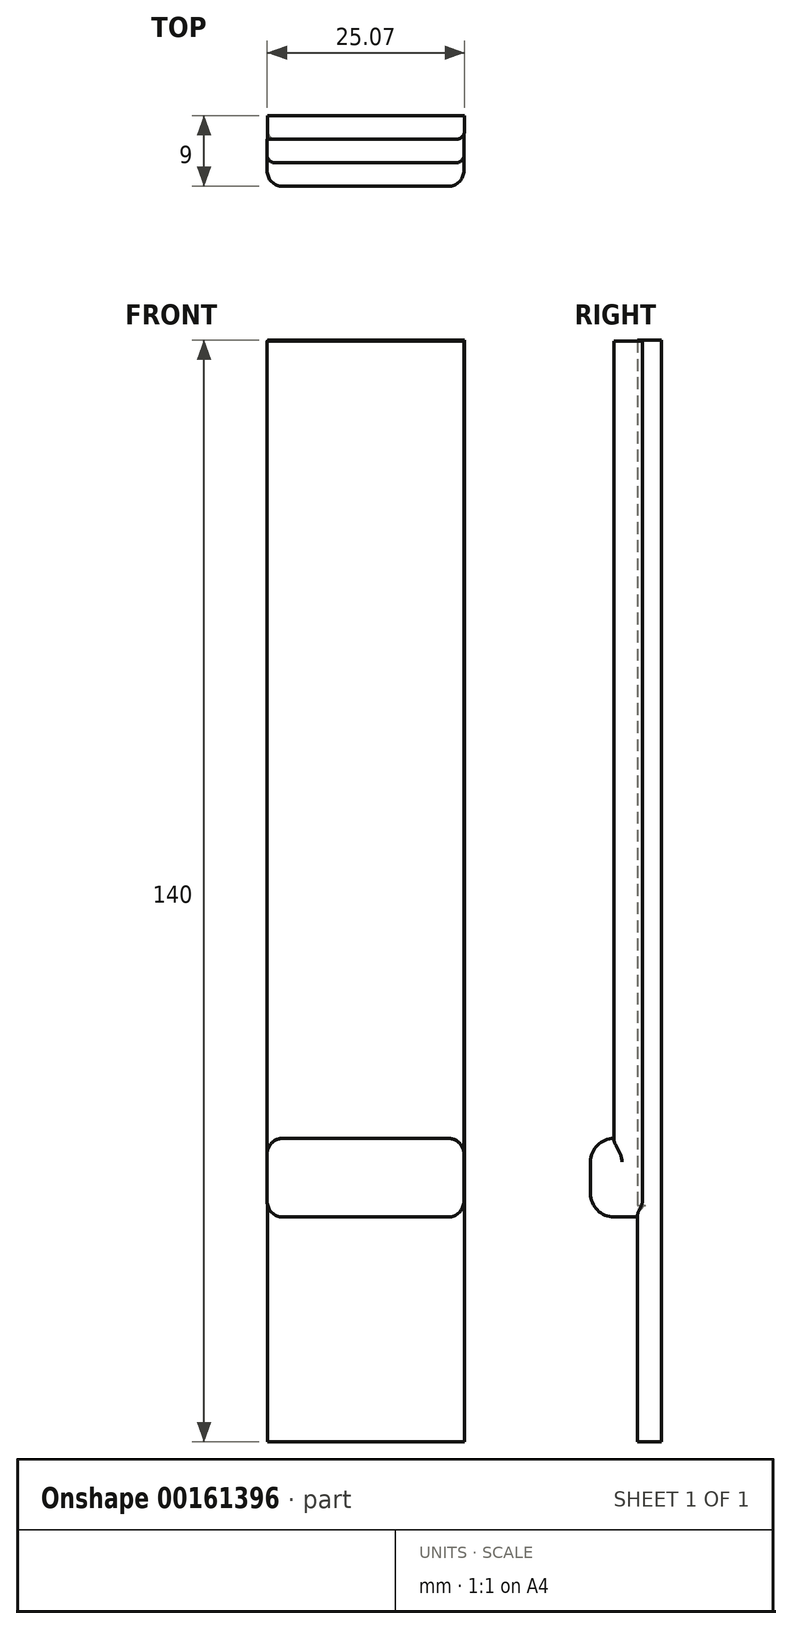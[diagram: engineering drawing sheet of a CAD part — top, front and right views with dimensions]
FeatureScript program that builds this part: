
annotation { "Feature Type Name" : "Feature", "Feature Type Description" : "" }
export const myFeature = defineFeature(function(context is Context, id is Id, definition is map)
    precondition{}
    {
        {
            var Q0;
            Q0=qCreatedBy(makeId("Front.planeOp"),FACE);
            var sketch = newSketch(context, id + "F0", { "sketchPlane" : qUnion([Q0])});
            skLineSegment(sketch, "E0.bottom", {"start": v(-25.63, 65.25) * mm, "end": v(-0.63, 65.25) * mm});
            skLineSegment(sketch, "E0.top", {"start": v(-25.63, -74.75) * mm, "end": v(-0.63, -74.75) * mm});
            skLineSegment(sketch, "E0.left", {"start": v(-25.63, 65.25) * mm, "end": v(-25.63, -74.75) * mm});
            skLineSegment(sketch, "E0.right", {"start": v(-0.63, 65.25) * mm, "end": v(-0.63, -74.75) * mm});
            skSolve(sketch);
        }
        {
            var Q0;
            Q0 = qSketchRegion(id + "F0", true);
            extrude(context, id + "F1", {"entities" : qUnion([Q0]), "depth" : 3 * mm});
        }
        {
            var Q0;
            Q0=makeQuery(id+"F1.opExtrude","CAP_FACE",FACE,{"disambiguationData":[OSD([sQuery(id+"F0.wireOp",EDGE,"E0.bottom"),sQuery(id+"F0.wireOp",EDGE,"E0.top"),sQuery(id+"F0.wireOp",EDGE,"E0.left"),sQuery(id+"F0.wireOp",EDGE,"E0.right")])],"isStart":false});
            var sketch = newSketch(context, id + "F2", { "sketchPlane" : qUnion([Q0])});
            skLineSegment(sketch, "E1.bottom", {"start": v(-25.7, 65.1) * mm, "end": v(-0.7, 65.1) * mm});
            skLineSegment(sketch, "E1.top", {"start": v(-25.7, -46.18) * mm, "end": v(-0.7, -46.18) * mm});
            skLineSegment(sketch, "E1.left", {"start": v(-25.7, 65.1) * mm, "end": v(-25.7, -46.18) * mm});
            skLineSegment(sketch, "E1.right", {"start": v(-0.7, 65.1) * mm, "end": v(-0.7, -46.18) * mm});
            skSolve(sketch);
        }
        {
            var Q0;
            Q0 = qSketchRegion(id + "F2", true);
            extrude(context, id + "F3", {"entities" : qUnion([Q0]), "operationType" : NewBodyOperationType.ADD, "depth" : 3 * mm});
        }
        {
            var Q0;
            Q0=makeQuery(id+"F3.opExtrude","CAP_FACE",FACE,{"disambiguationData":[OSD([sQuery(id+"F2.wireOp",EDGE,"E1.bottom"),sQuery(id+"F2.wireOp",EDGE,"E1.top"),sQuery(id+"F2.wireOp",EDGE,"E1.left"),sQuery(id+"F2.wireOp",EDGE,"E1.right")])],"isStart":false});
            var sketch = newSketch(context, id + "F4", { "sketchPlane" : qUnion([Q0])});
            skLineSegment(sketch, "E2.bottom", {"start": v(-25.7, -46.18) * mm, "end": v(-0.7, -46.18) * mm});
            skLineSegment(sketch, "E2.top", {"start": v(-25.7, -36.18) * mm, "end": v(-0.7, -36.18) * mm});
            skLineSegment(sketch, "E2.left", {"start": v(-25.7, -46.18) * mm, "end": v(-25.7, -36.18) * mm});
            skLineSegment(sketch, "E2.right", {"start": v(-0.7, -46.18) * mm, "end": v(-0.7, -36.18) * mm});
            skSolve(sketch);
        }
        {
            var Q0;
            Q0 = qSketchRegion(id + "F4", true);
            extrude(context, id + "F5", {"entities" : qUnion([Q0]), "operationType" : NewBodyOperationType.ADD, "depth" : 3 * mm});
        }
        {
            var Q0;
            Q0=makeQuery(id+"F5.opExtrude","CAP_EDGE",EDGE,{"disambiguationData":[OSD([sQuery(id+"F4.wireOp",EDGE,"E2.top")])],"isStart":false});
            var Q1;
            Q1=makeQuery(id+"F5.opExtrude","CAP_EDGE",EDGE,{"disambiguationData":[OSD([sQuery(id+"F4.wireOp",EDGE,"E2.bottom")])],"isStart":false});
            fillet(context, id + "F6", {"entities" : qUnion([Q0, Q1]), "radius" : 3 * mm, "tangentPropagation" : true, "allowEdgeOverflow" : false});
        }
        {
            var Q0;
            Q0=makeQuery(id+"F5.opExtrude","CAP_EDGE",EDGE,{"disambiguationData":[OSD([sQuery(id+"F4.wireOp",EDGE,"E2.left")])],"isStart":false});
            var Q1;
            Q1=makeQuery(id+"F5.opExtrude","CAP_EDGE",EDGE,{"disambiguationData":[OSD([sQuery(id+"F4.wireOp",EDGE,"E2.right")])],"isStart":false});
            fillet(context, id + "F7", {"entities" : qUnion([Q0, Q1]), "radius" : 2 * mm, "tangentPropagation" : true, "allowEdgeOverflow" : false});
        }
        {
            var Q0;
            Q0=makeQuery(id+"F3.opExtrude","CAP_EDGE",EDGE,{"disambiguationData":[OSD([sQuery(id+"F2.wireOp",EDGE,"E1.left")])],"isStart":false});
            var Q1;
            Q1=makeQuery(id+"F3.opExtrude","CAP_EDGE",EDGE,{"disambiguationData":[OSD([sQuery(id+"F2.wireOp",EDGE,"E1.right")])],"isStart":false});
            var Q2;
            {var subQ0=sQuery(id+"F2.wireOp",EDGE,"E1.top");var subQ1=sQuery(id+"F2.wireOp",EDGE,"E1.bottom");var subQ2=makeQuery(id+"F3.opExtrude","CAP_FACE",FACE,{"disambiguationData":[OSD([subQ1,subQ0,sQuery(id+"F2.wireOp",EDGE,"E1.left"),sQuery(id+"F2.wireOp",EDGE,"E1.right")])],"isStart":true});var subQ3=sQuery(id+"F0.wireOp",EDGE,"E0.left");var subQ4=makeQuery(id+"F1.opExtrude","SWEPT_FACE",FACE,{"disambiguationData":[OSD([subQ3])]});var subQ5=sQuery(id+"F0.wireOp",EDGE,"E0.top");var subQ6=makeQuery(id+"F1.opExtrude","CAP_FACE",FACE,{"disambiguationData":[OSD([sQuery(id+"F0.wireOp",EDGE,"E0.bottom"),subQ5,subQ3,sQuery(id+"F0.wireOp",EDGE,"E0.right")])],"isStart":false});var subQ7=makeQuery(id+"F3.opExtrude","SWEPT_FACE",FACE,{"disambiguationData":[OSD([subQ0])]});var subQ8=makeQuery(id+"F1.opExtrude","CAP_EDGE",EDGE,{"disambiguationData":[OSD([subQ3])],"isStart":false});Q2=makeQuery(id+"F7.opFillet","MERGE",EDGE,{"derivedFrom":[makeQuery(id+"F3.boolean.opBoolean","SPLIT",EDGE,{"disambiguationData":[TD([subQ6,makeQuery(id+"F1.opExtrude","SWEPT_FACE",FACE,{"disambiguationData":[OSD([subQ5])]}),subQ4,subQ2,subQ7])],"derivedFrom":subQ8}),makeQuery(id+"F3.boolean.opBoolean","SPLIT",EDGE,{"disambiguationData":[TD([subQ6,subQ4,makeQuery(id+"F3.opExtrude","SWEPT_FACE",FACE,{"disambiguationData":[OSD([subQ1])]}),subQ2,subQ7])],"derivedFrom":subQ8})]});}
            var Q3;
            Q3=makeQuery(id+"F1.opExtrude","CAP_EDGE",EDGE,{"disambiguationData":[OSD([sQuery(id+"F0.wireOp",EDGE,"E0.right")])],"isStart":false});
            fillet(context, id + "F8", {"entities" : qUnion([Q0, Q1, Q2, Q3]), "radius" : 1 * mm, "tangentPropagation" : true, "allowEdgeOverflow" : false});
        }
    });
